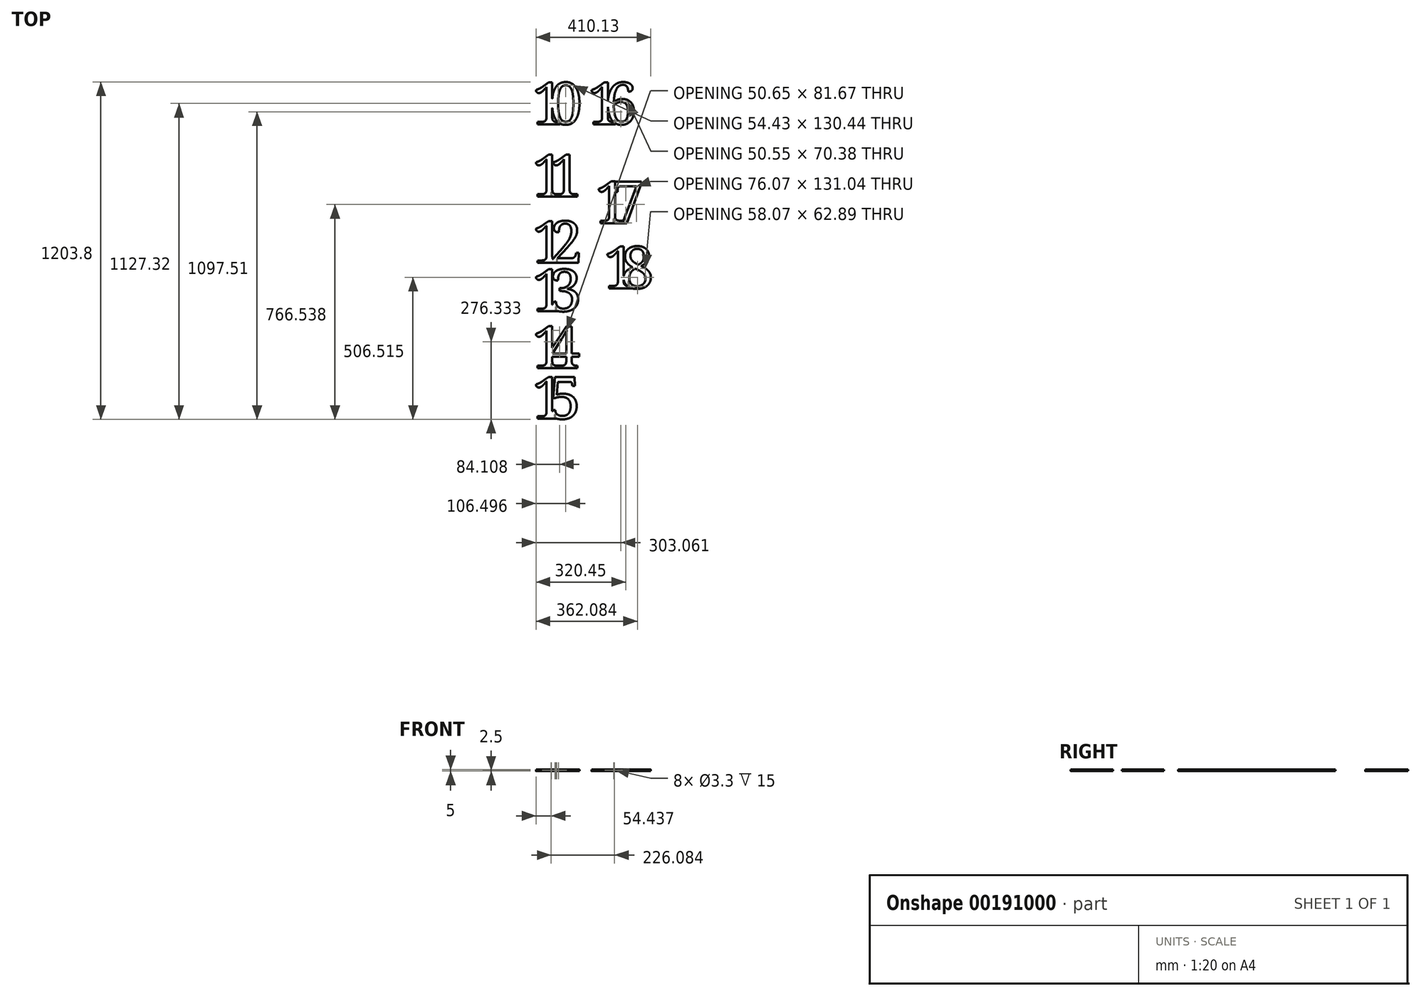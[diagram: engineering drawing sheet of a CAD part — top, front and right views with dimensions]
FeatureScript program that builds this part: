
annotation { "Feature Type Name" : "Feature", "Feature Type Description" : "" }
export const myFeature = defineFeature(function(context is Context, id is Id, definition is map)
    precondition{}
    {
        {
            var Q0;
            Q0=qCreatedBy(makeId("Top.planeOp"),FACE);
            var sketch = newSketch(context, id + "F0", { "sketchPlane" : qUnion([Q0])});
            skText(sketch, "E0", { "text": "1", "fontName": "NotoSerif-Regular.ttf"});
            skText(sketch, "E1", { "text": "0", "fontName": "NotoSerif-Regular.ttf"});
            const initialGuessF0  = {"E0": [0, 0, 1, 0, 0.15], "E1": [0.062, 0, 1, 0, 0.15]};
            skSetInitialGuess(sketch, initialGuessF0);
            skSolve(sketch);
        }
        {
            var Q0;
            Q0=makeQuery(id+"F0.imprint","IMPRINT",FACE,{"disambiguationData":[TD([[makeQuery(id+"F0.imprint","IMPRINT",EDGE,{"derivedFrom":sQuery(id+"F0.wireOp",EDGE,"E1.sketch_text.stroke-0")}),-1.0]])]});
            var Q1;
            Q1=makeQuery(id+"F0.imprint","IMPRINT",FACE,{"disambiguationData":[TD([[makeQuery(id+"F0.imprint","IMPRINT",EDGE,{"derivedFrom":sQuery(id+"F0.wireOp",EDGE,"E0.sketch_text.stroke-0")}),-1.0]])]});
            var Q2;
            {var subQ0=sQuery(id+"F0.wireOp",EDGE,"E0.sketch_text.stroke-25");var subQ1=sQuery(id+"F0.wireOp",EDGE,"E0.sketch_text.stroke-24");var subQ2=makeQuery(id+"F0.imprint","INTERSECT",VERTEX,{"derivedFrom":[subQ1,subQ0]});Q2=makeQuery(id+"F0.imprint","IMPRINT",FACE,{"disambiguationData":[TD([[makeQuery(id+"F0.imprint","IMPRINT",EDGE,{"disambiguationData":[TD([[subQ2,1.0]])],"derivedFrom":subQ1}),-1.0]])]});}
            var Q3;
            {var subQ0=sQuery(id+"F0.wireOp",EDGE,"E1.sketch_text.stroke-8");var subQ1=sQuery(id+"F0.wireOp",EDGE,"E0.sketch_text.stroke-19");var subQ2=makeQuery(id+"F0.imprint","INTERSECT",VERTEX,{"derivedFrom":[subQ1,subQ0]});Q3=makeQuery(id+"F0.imprint","IMPRINT",FACE,{"disambiguationData":[TD([[makeQuery(id+"F0.imprint","IMPRINT",EDGE,{"disambiguationData":[TD([[subQ2,-1.0]])],"derivedFrom":subQ1}),-1.0]])]});}
            extrude(context, id + "F1", {"entities" : qUnion([Q0, Q1, Q2, Q3]), "depth" : 5 * mm});
        }
        {
            var Q0;
            Q0=makeQuery(id+"F1.opExtrude","SWEPT_FACE",FACE,{"disambiguationData":[OSD([sQuery(id+"F0.wireOp",EDGE,"E0.sketch_text.stroke-26")])]});
            var sketch = newSketch(context, id + "F2", { "sketchPlane" : qUnion([Q0])});
            skCircle(sketch, "E2", {"center": v(94.63, 2.5) * mm, "radius": 1.65 * mm});
            skPoint(sketch, "E2.centerSnap0", {"position": v(99.38, 2.5) * mm});
            skSolve(sketch);
        }
        {
            var Q0;
            Q0 = qSketchRegion(id + "F2", true);
            extrude(context, id + "F3", {"entities" : qUnion([Q0]), "operationType" : NewBodyOperationType.REMOVE, "oppositeDirection" : true, "depth" : 15 * mm});
        }
        {
            var Q0;
            Q0=qCreatedBy(makeId("Top.planeOp"),FACE);
            var sketch = newSketch(context, id + "F4", { "sketchPlane" : qUnion([Q0])});
            skText(sketch, "E3", { "text": "1", "fontName": "NotoSerif-Regular.ttf"});
            skText(sketch, "E4", { "text": "1", "fontName": "NotoSerif-Regular.ttf"});
            const initialGuessF4  = {"E3": [0, -0.25813, 1, 0, 0.15], "E4": [0.062, -0.25813, 1, 0, 0.15]};
            skSetInitialGuess(sketch, initialGuessF4);
            skSolve(sketch);
        }
        {
            var Q0;
            Q0 = qSketchRegion(id + "F4", true);
            extrude(context, id + "F5", {"entities" : qUnion([Q0]), "depth" : 5 * mm});
        }
        {
            var Q0;
            Q0=makeQuery(id+"F5.opExtrude","SWEPT_FACE",FACE,{"disambiguationData":[OSD([sQuery(id+"F4.wireOp",EDGE,"E3.sketch_text.stroke-26"),sQuery(id+"F4.wireOp",EDGE,"E4.sketch_text.stroke-26")])]});
            var sketch = newSketch(context, id + "F6", { "sketchPlane" : qUnion([Q0])});
            skCircle(sketch, "E5", {"center": v(68.18, 2.5) * mm, "radius": 1.65 * mm});
            skPoint(sketch, "E5.centerSnap0", {"position": v(20.05, 2.5) * mm});
            skSolve(sketch);
        }
        {
            var Q0;
            Q0 = qSketchRegion(id + "F6", true);
            extrude(context, id + "F7", {"entities" : qUnion([Q0]), "operationType" : NewBodyOperationType.REMOVE, "oppositeDirection" : true, "depth" : 15 * mm});
        }
        {
            var Q0;
            Q0=qCreatedBy(makeId("Top.planeOp"),FACE);
            var sketch = newSketch(context, id + "F8", { "sketchPlane" : qUnion([Q0])});
            skText(sketch, "E6", { "text": "1", "fontName": "NotoSerif-Regular.ttf"});
            skText(sketch, "E7", { "text": "2", "fontName": "NotoSerif-Regular.ttf"});
            const initialGuessF8  = {"E6": [0, -0.49475, 1, 0, 0.15], "E7": [0.065, -0.49475, 1, 0, 0.15]};
            skSetInitialGuess(sketch, initialGuessF8);
            skSolve(sketch);
        }
        {
            var Q0;
            Q0 = qSketchRegion(id + "F8", true);
            extrude(context, id + "F9", {"entities" : qUnion([Q0]), "depth" : 5 * mm});
        }
        {
            var Q0;
            Q0=makeQuery(id+"F9.opExtrude","SWEPT_FACE",FACE,{"disambiguationData":[OSD([sQuery(id+"F8.wireOp",EDGE,"E6.sketch_text.stroke-26"),sQuery(id+"F8.wireOp",EDGE,"E7.sketch_text.stroke-13")])]});
            var sketch = newSketch(context, id + "F10", { "sketchPlane" : qUnion([Q0])});
            skCircle(sketch, "E8", {"center": v(87.88, 2.5) * mm, "radius": 1.65 * mm});
            skPoint(sketch, "E8.centerSnap0", {"position": v(20.05, 2.5) * mm});
            skSolve(sketch);
        }
        {
            var Q0;
            Q0 = qSketchRegion(id + "F10", true);
            extrude(context, id + "F11", {"entities" : qUnion([Q0]), "operationType" : NewBodyOperationType.REMOVE, "oppositeDirection" : true, "depth" : 15 * mm});
        }
        {
            var Q0;
            Q0=qCreatedBy(makeId("Top.planeOp"),FACE);
            var sketch = newSketch(context, id + "F12", { "sketchPlane" : qUnion([Q0])});
            skText(sketch, "E9", { "text": "1", "fontName": "NotoSerif-Regular.ttf"});
            skText(sketch, "E10", { "text": "3", "fontName": "NotoSerif-Regular.ttf"});
            const initialGuessF12  = {"E9": [0, -0.66686, 1, 0, 0.15], "E10": [0.06, -0.66686, 1, 0, 0.15]};
            skSetInitialGuess(sketch, initialGuessF12);
            skSolve(sketch);
        }
        {
            var Q0;
            Q0 = qSketchRegion(id + "F12", true);
            extrude(context, id + "F13", {"entities" : qUnion([Q0]), "depth" : 5 * mm});
        }
        {
            var Q0;
            Q0=makeQuery(id+"F13.opExtrude","SWEPT_FACE",FACE,{"disambiguationData":[OSD([sQuery(id+"F12.wireOp",EDGE,"E9.sketch_text.stroke-26")])]});
            var sketch = newSketch(context, id + "F14", { "sketchPlane" : qUnion([Q0])});
            skCircle(sketch, "E11", {"center": v(85.27, 2.5) * mm, "radius": 1.65 * mm});
            skPoint(sketch, "E11.centerSnap0", {"position": v(93.15, 2.5) * mm});
            skSolve(sketch);
        }
        {
            var Q0;
            Q0 = qSketchRegion(id + "F14", true);
            extrude(context, id + "F15", {"entities" : qUnion([Q0]), "operationType" : NewBodyOperationType.REMOVE, "oppositeDirection" : true, "depth" : 15 * mm});
        }
        {
            var Q0;
            Q0=qCreatedBy(makeId("Top.planeOp"),FACE);
            var sketch = newSketch(context, id + "F16", { "sketchPlane" : qUnion([Q0])});
            skText(sketch, "E12", { "text": "1", "fontName": "NotoSerif-Regular.ttf"});
            skText(sketch, "E13", { "text": "4", "fontName": "NotoSerif-Regular.ttf"});
            const initialGuessF16  = {"E12": [0, -0.86996, 1, 0, 0.15], "E13": [0.054, -0.86996, 1, 0, 0.15]};
            skSetInitialGuess(sketch, initialGuessF16);
            skSolve(sketch);
        }
        {
            var Q0;
            Q0 = qSketchRegion(id + "F16", true);
            extrude(context, id + "F17", {"entities" : qUnion([Q0]), "depth" : 5 * mm});
        }
        {
            var Q0;
            Q0=makeQuery(id+"F17.opExtrude","SWEPT_FACE",FACE,{"disambiguationData":[OSD([sQuery(id+"F16.wireOp",EDGE,"E12.sketch_text.stroke-26"),sQuery(id+"F16.wireOp",EDGE,"E13.sketch_text.stroke-7")])]});
            var sketch = newSketch(context, id + "F18", { "sketchPlane" : qUnion([Q0])});
            skCircle(sketch, "E14", {"center": v(68.63, 2.5) * mm, "radius": 1.65 * mm});
            skPoint(sketch, "E14.centerSnap0", {"position": v(20.05, 2.5) * mm});
            skSolve(sketch);
        }
        {
            var Q0;
            Q0 = qSketchRegion(id + "F18", true);
            extrude(context, id + "F19", {"entities" : qUnion([Q0]), "operationType" : NewBodyOperationType.REMOVE, "oppositeDirection" : true, "depth" : 15 * mm});
        }
        {
            var Q0;
            Q0=qCreatedBy(makeId("Top.planeOp"),FACE);
            var sketch = newSketch(context, id + "F20", { "sketchPlane" : qUnion([Q0])});
            skText(sketch, "E15", { "text": "1", "fontName": "NotoSerif-Regular.ttf"});
            skText(sketch, "E16", { "text": "5", "fontName": "NotoSerif-Regular.ttf"});
            const initialGuessF20  = {"E15": [0, -1.0509, 1, 0, 0.15], "E16": [0.058, -1.0509, 1, 0, 0.15]};
            skSetInitialGuess(sketch, initialGuessF20);
            skSolve(sketch);
        }
        {
            var Q0;
            Q0 = qSketchRegion(id + "F20", true);
            extrude(context, id + "F21", {"entities" : qUnion([Q0]), "depth" : 5 * mm});
        }
        {
            var Q0;
            Q0=makeQuery(id+"F21.opExtrude","SWEPT_FACE",FACE,{"disambiguationData":[OSD([sQuery(id+"F20.wireOp",EDGE,"E15.sketch_text.stroke-26")])]});
            var sketch = newSketch(context, id + "F22", { "sketchPlane" : qUnion([Q0])});
            skCircle(sketch, "E17", {"center": v(81.2, 2.5) * mm, "radius": 1.65 * mm});
            skPoint(sketch, "E17.centerSnap0", {"position": v(89.44, 2.5) * mm});
            skSolve(sketch);
        }
        {
            var Q0;
            Q0 = qSketchRegion(id + "F22", true);
            extrude(context, id + "F23", {"entities" : qUnion([Q0]), "operationType" : NewBodyOperationType.REMOVE, "oppositeDirection" : true, "depth" : 15 * mm});
        }
        {
            var Q0;
            Q0=qCreatedBy(makeId("Top.planeOp"),FACE);
            var sketch = newSketch(context, id + "F24", { "sketchPlane" : qUnion([Q0])});
            skText(sketch, "E18", { "text": "1", "fontName": "NotoSerif-Regular.ttf"});
            skText(sketch, "E19", { "text": "6", "fontName": "NotoSerif-Regular.ttf"});
            const initialGuessF24  = {"E18": [0.19854, 0, 1, 0, 0.15], "E19": [0.25754, 0, 1, 0, 0.15]};
            skSetInitialGuess(sketch, initialGuessF24);
            skSolve(sketch);
        }
        {
            var Q0;
            Q0 = qSketchRegion(id + "F24", true);
            extrude(context, id + "F25", {"entities" : qUnion([Q0]), "depth" : 5 * mm});
        }
        {
            var Q0;
            Q0=makeQuery(id+"F25.opExtrude","SWEPT_FACE",FACE,{"disambiguationData":[OSD([sQuery(id+"F24.wireOp",EDGE,"E18.sketch_text.stroke-26")])]});
            var sketch = newSketch(context, id + "F26", { "sketchPlane" : qUnion([Q0])});
            skCircle(sketch, "E20", {"center": v(294.26, 2.5) * mm, "radius": 1.65 * mm});
            skPoint(sketch, "E20.centerSnap0", {"position": v(297.92, 2.5) * mm});
            skSolve(sketch);
        }
        {
            var Q0;
            Q0 = qSketchRegion(id + "F26", true);
            extrude(context, id + "F27", {"entities" : qUnion([Q0]), "operationType" : NewBodyOperationType.REMOVE, "oppositeDirection" : true, "depth" : 15 * mm});
        }
        {
            var Q0;
            Q0=qCreatedBy(makeId("Top.planeOp"),FACE);
            var sketch = newSketch(context, id + "F28", { "sketchPlane" : qUnion([Q0])});
            skText(sketch, "E21", { "text": "1", "fontName": "NotoSerif-Regular.ttf"});
            skText(sketch, "E22", { "text": "7", "fontName": "NotoSerif-Regular.ttf"});
            const initialGuessF28  = {"E21": [0.22402, -0.35273, 1, 0, 0.15], "E22": [0.28352, -0.35273, 1, 0, 0.15]};
            skSetInitialGuess(sketch, initialGuessF28);
            skSolve(sketch);
        }
        {
            var Q0;
            Q0 = qSketchRegion(id + "F28", true);
            extrude(context, id + "F29", {"entities" : qUnion([Q0]), "depth" : 5 * mm});
        }
        {
            var Q0;
            Q0=makeQuery(id+"F29.opExtrude","SWEPT_FACE",FACE,{"disambiguationData":[OSD([sQuery(id+"F28.wireOp",EDGE,"E21.sketch_text.stroke-26"),sQuery(id+"F28.wireOp",EDGE,"E22.sketch_text.stroke-9")])]});
            var sketch = newSketch(context, id + "F30", { "sketchPlane" : qUnion([Q0])});
            skCircle(sketch, "E23", {"center": v(290.93, 2.5) * mm, "radius": 1.65 * mm});
            skPoint(sketch, "E23.centerSnap0", {"position": v(244.07, 2.5) * mm});
            skSolve(sketch);
        }
        {
            var Q0;
            Q0 = qSketchRegion(id + "F30", true);
            extrude(context, id + "F31", {"entities" : qUnion([Q0]), "operationType" : NewBodyOperationType.REMOVE, "oppositeDirection" : true, "depth" : 15 * mm});
        }
        {
            var Q0;
            Q0=qCreatedBy(makeId("Top.planeOp"),FACE);
            var sketch = newSketch(context, id + "F32", { "sketchPlane" : qUnion([Q0])});
            skText(sketch, "E24", { "text": "1", "fontName": "NotoSerif-Regular.ttf"});
            skText(sketch, "E25", { "text": "8", "fontName": "NotoSerif-Regular.ttf"});
            const initialGuessF32  = {"E24": [0.25497, -0.5854, 1, 0, 0.15], "E25": [0.31697, -0.5854, 1, 0, 0.15]};
            skSetInitialGuess(sketch, initialGuessF32);
            skSolve(sketch);
        }
        {
            var Q0;
            Q0 = qSketchRegion(id + "F32", true);
            extrude(context, id + "F33", {"entities" : qUnion([Q0]), "depth" : 5 * mm});
        }
        {
            var Q0;
            Q0=makeQuery(id+"F33.opExtrude","SWEPT_FACE",FACE,{"disambiguationData":[OSD([sQuery(id+"F32.wireOp",EDGE,"E24.sketch_text.stroke-26")])]});
            var sketch = newSketch(context, id + "F34", { "sketchPlane" : qUnion([Q0])});
            skCircle(sketch, "E26", {"center": v(344.21, 2.5) * mm, "radius": 1.65 * mm});
            skPoint(sketch, "E26.centerSnap0", {"position": v(354.35, 2.5) * mm});
            skSolve(sketch);
        }
        {
            var Q0;
            Q0 = qSketchRegion(id + "F34", true);
            extrude(context, id + "F35", {"entities" : qUnion([Q0]), "operationType" : NewBodyOperationType.REMOVE, "oppositeDirection" : true, "depth" : 25 * mm});
        }
    });
